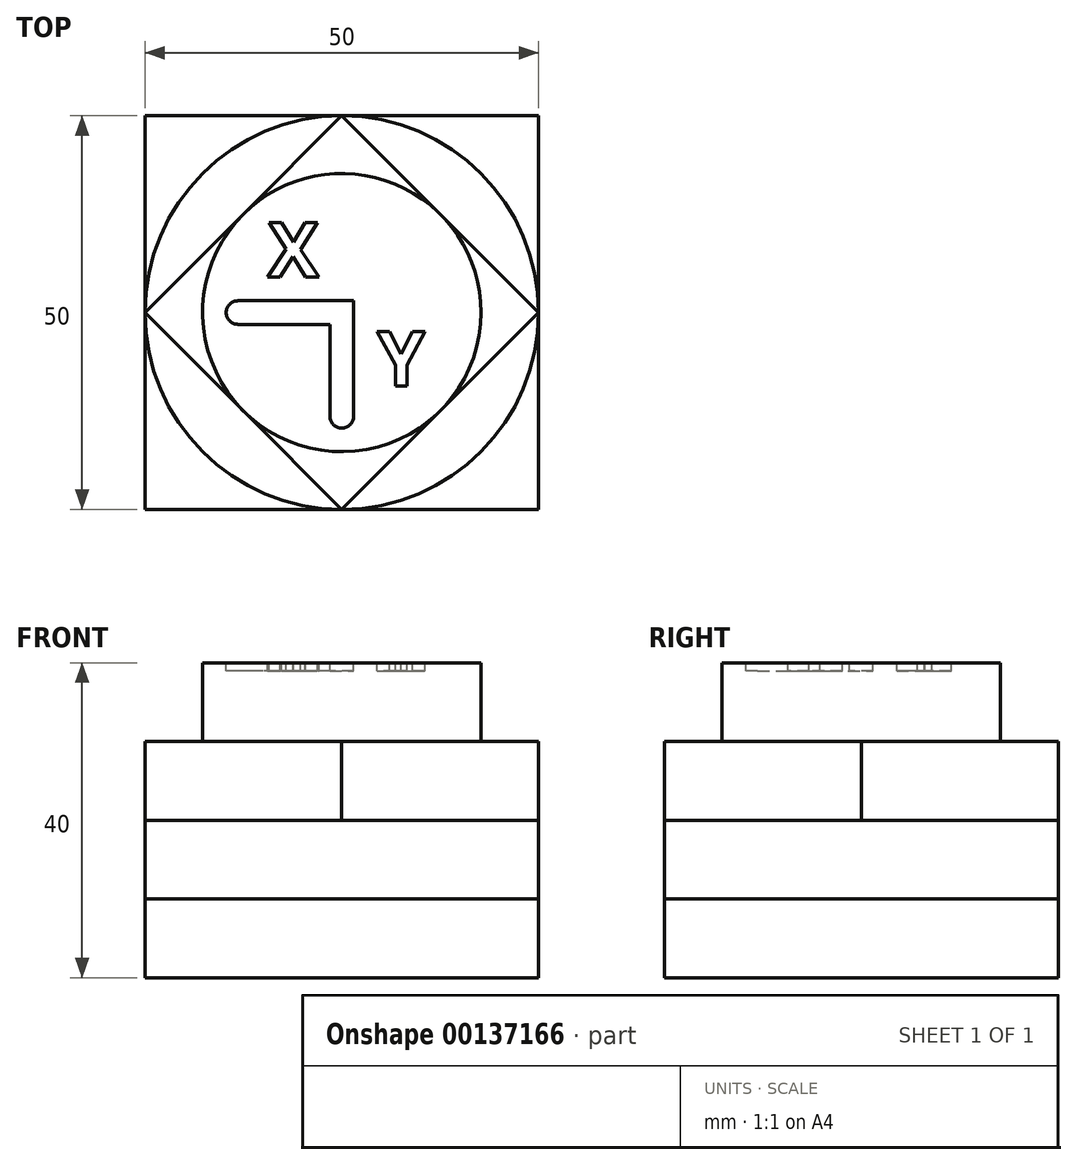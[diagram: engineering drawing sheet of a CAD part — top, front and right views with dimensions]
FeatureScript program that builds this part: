
annotation { "Feature Type Name" : "Feature", "Feature Type Description" : "" }
export const myFeature = defineFeature(function(context is Context, id is Id, definition is map)
    precondition{}
    {
        {
            var Q0;
            Q0=qCreatedBy(makeId("Top.planeOp"),FACE);
            var sketch = newSketch(context, id + "F0", { "sketchPlane" : qUnion([Q0])});
            skLineSegment(sketch, "E0.bottom", {"start": v(25, 25) * mm, "end": v(-25, 25) * mm});
            skLineSegment(sketch, "E0.top", {"start": v(25, -25) * mm, "end": v(-25, -25) * mm});
            skLineSegment(sketch, "E0.left", {"start": v(25, 25) * mm, "end": v(25, -25) * mm});
            skLineSegment(sketch, "E0.right", {"start": v(-25, 25) * mm, "end": v(-25, -25) * mm});
            skCircle(sketch, "E1", {"center": v(0, 0) * mm, "radius": 25 * mm});
            skLineSegment(sketch, "E2", {"start": v(-25, 0) * mm, "end": v(0, 25) * mm});
            skLineSegment(sketch, "E3", {"start": v(0, 25) * mm, "end": v(25, 0) * mm});
            skLineSegment(sketch, "E4", {"start": v(25, 0) * mm, "end": v(0, -25) * mm});
            skLineSegment(sketch, "E5", {"start": v(0, -25) * mm, "end": v(-25, 0) * mm});
            skCircle(sketch, "E6", {"center": v(0, 0) * mm, "radius": 17.68 * mm});
            skSolve(sketch);
        }
        {
            var Q0;
            Q0 = qSketchRegion(id + "F0", true);
            var Q1;
            Q1=makeQuery(id+"F0.imprint","IMPRINT",FACE,{"disambiguationData":[TD([[makeQuery(id+"F0.imprint","IMPRINT",EDGE,{"derivedFrom":sQuery(id+"F0.wireOp",EDGE,"79ae97e4-c3c9-419f-b08e-7ab59219a8d8.sketch_text.stroke-0")}),1.0]])]});
            var Q2;
            {var subQ0=sQuery(id+"F0.wireOp",EDGE,"In16kzxK-pmkk-qiK2-19Kq-upd4eBiPAnsH");Q2=makeQuery(id+"F0.imprint","IMPRINT",FACE,{"disambiguationData":[TD([[makeQuery(id+"F0.imprint","IMPRINT",EDGE,{"derivedFrom":subQ0}),1.0]])]});}
            var Q3;
            Q3=makeQuery(id+"F0.imprint","IMPRINT",FACE,{"disambiguationData":[TD([[makeQuery(id+"F0.imprint","IMPRINT",EDGE,{"derivedFrom":sQuery(id+"F0.wireOp",EDGE,"79ae97e4-c3c9-419f-b08e-7ab59219a8d8.sketch_text.stroke-0")}),-1.0]])]});
            var Q4;
            Q4=makeQuery(id+"F0.imprint","IMPRINT",FACE,{"disambiguationData":[TD([[makeQuery(id+"F0.imprint","IMPRINT",EDGE,{"derivedFrom":sQuery(id+"F0.wireOp",EDGE,"0fed53cb-6c0c-4cfe-9a05-34acf5c978ca.sketch_text.stroke-0")}),-1.0]])]});
            var Q5;
            {var subQ5=sQuery(id+"F0.wireOp",EDGE,"59whxODq-4lG4-uGw3-aSl6-LnsZHjYmxgPS");Q5=makeQuery(id+"F0.imprint","IMPRINT",FACE,{"disambiguationData":[TD([[makeQuery(id+"F0.imprint","IMPRINT",EDGE,{"derivedFrom":subQ5}),1.0]])]});}
            var Q6;
            {var subQ0=sQuery(id+"F0.wireOp",EDGE,"59whxODq-4lG4-uGw3-aSl6-LnsZHjYmxgPS");Q6=makeQuery(id+"F0.imprint","IMPRINT",FACE,{"disambiguationData":[TD([[makeQuery(id+"F0.imprint","IMPRINT",EDGE,{"derivedFrom":subQ0}),-1.0]])]});}
            var Q7;
            {var subQ2=sQuery(id+"F0.wireOp",EDGE,"0j6AniGb-W7Nw-E4wu-Dbwd-GDOL3unB0ds2");Q7=makeQuery(id+"F0.imprint","IMPRINT",FACE,{"disambiguationData":[TD([[makeQuery(id+"F0.imprint","IMPRINT",EDGE,{"derivedFrom":subQ2}),1.0]])]});}
            var Q8;
            {var subQ1=sQuery(id+"F0.wireOp",EDGE,"In16kzxK-pmkk-qiK2-19Kq-upd4eBiPAnsH");Q8=makeQuery(id+"F0.imprint","IMPRINT",FACE,{"disambiguationData":[TD([[makeQuery(id+"F0.imprint","IMPRINT",EDGE,{"derivedFrom":subQ1}),-1.0]])]});}
            var Q9;
            {var subQ1=sQuery(id+"F0.wireOp",EDGE,"pZ83yii7-nPWr-2Kfu-6QAO-RtWfx2XcWZdh.top");var subQ3=sQuery(id+"F0.wireOp",EDGE,"EnXiYws3-z1Fz-EJbT-Ovdj-ZJikFFibwCy3.right");var subQ4=makeQuery(id+"F0.imprint","INTERSECT",VERTEX,{"derivedFrom":[subQ1,subQ3]});Q9=makeQuery(id+"F0.imprint","IMPRINT",FACE,{"disambiguationData":[TD([[makeQuery(id+"F0.imprint","IMPRINT",EDGE,{"disambiguationData":[TD([[subQ4,1.0]])],"derivedFrom":subQ1}),-1.0]])]});}
            var Q10;
            {var subQ0=sQuery(id+"F0.wireOp",EDGE,"HMWayQ6C-GFmY-SrYf-xaED-6YKDjYhzZWfb");Q10=makeQuery(id+"F0.imprint","IMPRINT",FACE,{"disambiguationData":[TD([[makeQuery(id+"F0.imprint","IMPRINT",EDGE,{"derivedFrom":subQ0}),1.0]])]});}
            var Q11;
            {var subQ2=sQuery(id+"F0.wireOp",EDGE,"QxC8kKsA-oIuu-Nvzd-oggT-BD9SnXOtptM4");Q11=makeQuery(id+"F0.imprint","IMPRINT",FACE,{"disambiguationData":[TD([[makeQuery(id+"F0.imprint","IMPRINT",EDGE,{"derivedFrom":subQ2}),1.0]])]});}
            var Q12;
            {var subQ0=sQuery(id+"F0.wireOp",EDGE,"E6");var subQ1=makeQuery(id+"F0.imprint","INTERSECT",VERTEX,{"derivedFrom":[sQuery(id+"F0.wireOp",EDGE,"E2"),subQ0]});Q12=makeQuery(id+"F0.imprint","IMPRINT",FACE,{"disambiguationData":[TD([[makeQuery(id+"F0.imprint","IMPRINT",EDGE,{"disambiguationData":[TD([[subQ1,1.0]])],"derivedFrom":subQ0}),1.0]])]});}
            extrude(context, id + "F1", {"entities" : qUnion([Q0, Q1, Q2, Q3, Q4, Q5, Q6, Q7, Q8, Q9, Q10, Q11, Q12]), "depth" : 10 * mm});
        }
        {
            var Q0;
            {var subQ0=sQuery(id+"F0.wireOp",EDGE,"E5");var subQ4=makeQuery(id+"F0.imprint","INTERSECT",VERTEX,{"derivedFrom":[subQ0,sQuery(id+"F0.wireOp",EDGE,"E6")]});Q0=makeQuery(id+"F0.imprint","IMPRINT",FACE,{"disambiguationData":[TD([[makeQuery(id+"F0.imprint","IMPRINT",EDGE,{"disambiguationData":[TD([[subQ4,1.0]])],"derivedFrom":subQ0}),1.0]])]});}
            var Q1;
            {var subQ0=sQuery(id+"F0.wireOp",EDGE,"E2");var subQ4=makeQuery(id+"F0.imprint","INTERSECT",VERTEX,{"derivedFrom":[subQ0,sQuery(id+"F0.wireOp",EDGE,"E6")]});Q1=makeQuery(id+"F0.imprint","IMPRINT",FACE,{"disambiguationData":[TD([[makeQuery(id+"F0.imprint","IMPRINT",EDGE,{"disambiguationData":[TD([[subQ4,1.0]])],"derivedFrom":subQ0}),1.0]])]});}
            var Q2;
            {var subQ0=sQuery(id+"F0.wireOp",EDGE,"E6");var subQ1=makeQuery(id+"F0.imprint","INTERSECT",VERTEX,{"derivedFrom":[sQuery(id+"F0.wireOp",EDGE,"E2"),subQ0]});Q2=makeQuery(id+"F0.imprint","IMPRINT",FACE,{"disambiguationData":[TD([[makeQuery(id+"F0.imprint","IMPRINT",EDGE,{"disambiguationData":[TD([[subQ1,1.0]])],"derivedFrom":subQ0}),1.0]])]});}
            var Q3;
            {var subQ0=sQuery(id+"F0.wireOp",EDGE,"E3");var subQ4=makeQuery(id+"F0.imprint","INTERSECT",VERTEX,{"derivedFrom":[subQ0,sQuery(id+"F0.wireOp",EDGE,"E6")]});Q3=makeQuery(id+"F0.imprint","IMPRINT",FACE,{"disambiguationData":[TD([[makeQuery(id+"F0.imprint","IMPRINT",EDGE,{"disambiguationData":[TD([[subQ4,1.0]])],"derivedFrom":subQ0}),1.0]])]});}
            var Q4;
            {var subQ0=sQuery(id+"F0.wireOp",EDGE,"E4");var subQ4=makeQuery(id+"F0.imprint","INTERSECT",VERTEX,{"derivedFrom":[subQ0,sQuery(id+"F0.wireOp",EDGE,"E6")]});Q4=makeQuery(id+"F0.imprint","IMPRINT",FACE,{"disambiguationData":[TD([[makeQuery(id+"F0.imprint","IMPRINT",EDGE,{"disambiguationData":[TD([[subQ4,1.0]])],"derivedFrom":subQ0}),1.0]])]});}
            var Q5;
            {var subQ1=sQuery(id+"F0.wireOp",EDGE,"E3");var subQ3=sQuery(id+"F0.wireOp",EDGE,"E6");var subQ4=makeQuery(id+"F0.imprint","INTERSECT",VERTEX,{"derivedFrom":[subQ1,subQ3]});Q5=makeQuery(id+"F0.imprint","IMPRINT",FACE,{"disambiguationData":[TD([[makeQuery(id+"F0.imprint","IMPRINT",EDGE,{"disambiguationData":[TD([[subQ4,1.0]])],"derivedFrom":subQ3}),-1.0]])]});}
            var Q6;
            {var subQ1=sQuery(id+"F0.wireOp",EDGE,"E4");var subQ3=sQuery(id+"F0.wireOp",EDGE,"E6");var subQ4=makeQuery(id+"F0.imprint","INTERSECT",VERTEX,{"derivedFrom":[subQ1,subQ3]});Q6=makeQuery(id+"F0.imprint","IMPRINT",FACE,{"disambiguationData":[TD([[makeQuery(id+"F0.imprint","IMPRINT",EDGE,{"disambiguationData":[TD([[subQ4,1.0]])],"derivedFrom":subQ3}),-1.0]])]});}
            var Q7;
            {var subQ1=sQuery(id+"F0.wireOp",EDGE,"E2");var subQ3=sQuery(id+"F0.wireOp",EDGE,"E6");var subQ4=makeQuery(id+"F0.imprint","INTERSECT",VERTEX,{"derivedFrom":[subQ1,subQ3]});Q7=makeQuery(id+"F0.imprint","IMPRINT",FACE,{"disambiguationData":[TD([[makeQuery(id+"F0.imprint","IMPRINT",EDGE,{"disambiguationData":[TD([[subQ4,-1.0]])],"derivedFrom":subQ3}),-1.0]])]});}
            var Q8;
            {var subQ1=sQuery(id+"F0.wireOp",EDGE,"E2");var subQ3=sQuery(id+"F0.wireOp",EDGE,"E6");var subQ4=makeQuery(id+"F0.imprint","INTERSECT",VERTEX,{"derivedFrom":[subQ1,subQ3]});Q8=makeQuery(id+"F0.imprint","IMPRINT",FACE,{"disambiguationData":[TD([[makeQuery(id+"F0.imprint","IMPRINT",EDGE,{"disambiguationData":[TD([[subQ4,1.0]])],"derivedFrom":subQ3}),-1.0]])]});}
            extrude(context, id + "F2", {"entities" : qUnion([Q0, Q1, Q2, Q3, Q4, Q5, Q6, Q7, Q8]), "operationType" : NewBodyOperationType.ADD, "depth" : 20 * mm});
        }
        {
            var Q0;
            {var subQ1=sQuery(id+"F0.wireOp",EDGE,"E4");var subQ3=sQuery(id+"F0.wireOp",EDGE,"E6");var subQ4=makeQuery(id+"F0.imprint","INTERSECT",VERTEX,{"derivedFrom":[subQ1,subQ3]});Q0=makeQuery(id+"F0.imprint","IMPRINT",FACE,{"disambiguationData":[TD([[makeQuery(id+"F0.imprint","IMPRINT",EDGE,{"disambiguationData":[TD([[subQ4,1.0]])],"derivedFrom":subQ3}),-1.0]])]});}
            var Q1;
            {var subQ1=sQuery(id+"F0.wireOp",EDGE,"E3");var subQ3=sQuery(id+"F0.wireOp",EDGE,"E6");var subQ4=makeQuery(id+"F0.imprint","INTERSECT",VERTEX,{"derivedFrom":[subQ1,subQ3]});Q1=makeQuery(id+"F0.imprint","IMPRINT",FACE,{"disambiguationData":[TD([[makeQuery(id+"F0.imprint","IMPRINT",EDGE,{"disambiguationData":[TD([[subQ4,1.0]])],"derivedFrom":subQ3}),-1.0]])]});}
            var Q2;
            {var subQ0=sQuery(id+"F0.wireOp",EDGE,"E6");var subQ1=makeQuery(id+"F0.imprint","INTERSECT",VERTEX,{"derivedFrom":[sQuery(id+"F0.wireOp",EDGE,"E2"),subQ0]});Q2=makeQuery(id+"F0.imprint","IMPRINT",FACE,{"disambiguationData":[TD([[makeQuery(id+"F0.imprint","IMPRINT",EDGE,{"disambiguationData":[TD([[subQ1,1.0]])],"derivedFrom":subQ0}),1.0]])]});}
            var Q3;
            {var subQ1=sQuery(id+"F0.wireOp",EDGE,"E2");var subQ3=sQuery(id+"F0.wireOp",EDGE,"E6");var subQ4=makeQuery(id+"F0.imprint","INTERSECT",VERTEX,{"derivedFrom":[subQ1,subQ3]});Q3=makeQuery(id+"F0.imprint","IMPRINT",FACE,{"disambiguationData":[TD([[makeQuery(id+"F0.imprint","IMPRINT",EDGE,{"disambiguationData":[TD([[subQ4,1.0]])],"derivedFrom":subQ3}),-1.0]])]});}
            var Q4;
            {var subQ1=sQuery(id+"F0.wireOp",EDGE,"E2");var subQ3=sQuery(id+"F0.wireOp",EDGE,"E6");var subQ4=makeQuery(id+"F0.imprint","INTERSECT",VERTEX,{"derivedFrom":[subQ1,subQ3]});Q4=makeQuery(id+"F0.imprint","IMPRINT",FACE,{"disambiguationData":[TD([[makeQuery(id+"F0.imprint","IMPRINT",EDGE,{"disambiguationData":[TD([[subQ4,-1.0]])],"derivedFrom":subQ3}),-1.0]])]});}
            extrude(context, id + "F3", {"entities" : qUnion([Q0, Q1, Q2, Q3, Q4]), "operationType" : NewBodyOperationType.ADD, "depth" : 30 * mm});
        }
        {
            var Q0;
            {var subQ0=sQuery(id+"F0.wireOp",EDGE,"E6");var subQ1=makeQuery(id+"F0.imprint","INTERSECT",VERTEX,{"derivedFrom":[sQuery(id+"F0.wireOp",EDGE,"E2"),subQ0]});Q0=makeQuery(id+"F0.imprint","IMPRINT",FACE,{"disambiguationData":[TD([[makeQuery(id+"F0.imprint","IMPRINT",EDGE,{"disambiguationData":[TD([[subQ1,1.0]])],"derivedFrom":subQ0}),1.0]])]});}
            extrude(context, id + "F4", {"entities" : qUnion([Q0]), "operationType" : NewBodyOperationType.ADD, "depth" : 40 * mm});
        }
        {
            var Q0;
            Q0=makeQuery(id+"F4.opExtrude","CAP_FACE",FACE,{"disambiguationData":[OSD([sQuery(id+"F0.wireOp",EDGE,"E6")])],"isStart":false});
            var sketch = newSketch(context, id + "F5", { "sketchPlane" : qUnion([Q0])});
            skLineSegment(sketch, "E7", {"start": v(1.5, -13.18) * mm, "end": v(1.5, 1.5) * mm});
            skLineSegment(sketch, "E8", {"start": v(1.5, 1.5) * mm, "end": v(-13.18, 1.5) * mm});
            skLineSegment(sketch, "E9", {"start": v(-1.5, -13.18) * mm, "end": v(-1.5, -1.5) * mm});
            skLineSegment(sketch, "E10", {"start": v(-1.5, -1.5) * mm, "end": v(-13.18, -1.5) * mm});
            skArc(sketch, "E11", {"start": v(-13.18, 1.5) * mm, "mid": v(-14.68, 0) * mm, "end": v(-13.18, -1.5) * mm});
            skArc(sketch, "E12", {"start": v(-1.5, -13.18) * mm, "mid": v(0, -14.68) * mm, "end": v(1.5, -13.18) * mm});
            skLineSegment(sketch, "E13", {"start": v(1.5, 1.5) * mm, "end": v(-1.5, -1.5) * mm, "construction": true});
            skPoint(sketch, "E14", {"position": v(0, 0) * mm});
            skPoint(sketch, "E15", {"position": v(-14.68, 0) * mm});
            skPoint(sketch, "E16", {"position": v(-17.68, 0) * mm});
            skPoint(sketch, "E17.visualSharp", {"position": v(1.5, 1.5) * mm});
            skText(sketch, "E18", { "text": "Y", "fontName": "OpenSans-Bold.ttf"});
            skPoint(sketch, "E19", {"position": v(4.5, -5.84) * mm});
            skPoint(sketch, "E20", {"position": v(1.5, -5.84) * mm});
            skText(sketch, "E21", { "text": "X", "fontName": "OpenSans-Bold.ttf"});
            skPoint(sketch, "E22", {"position": v(-5.84, 1.5) * mm});
            const initialGuessF5  = {"E18": [0.0045, -0.00934, 1, 0, 0.007], "E21": [-0.0094, 0.0045, 1, 0, 0.007]};
            skSetInitialGuess(sketch, initialGuessF5);
            skSolve(sketch);
        }
        {
            var Q0;
            Q0 = qSketchRegion(id + "F5", true);
            extrude(context, id + "F6", {"entities" : qUnion([Q0]), "operationType" : NewBodyOperationType.REMOVE, "oppositeDirection" : true, "depth" : 1 * mm});
        }
    });
